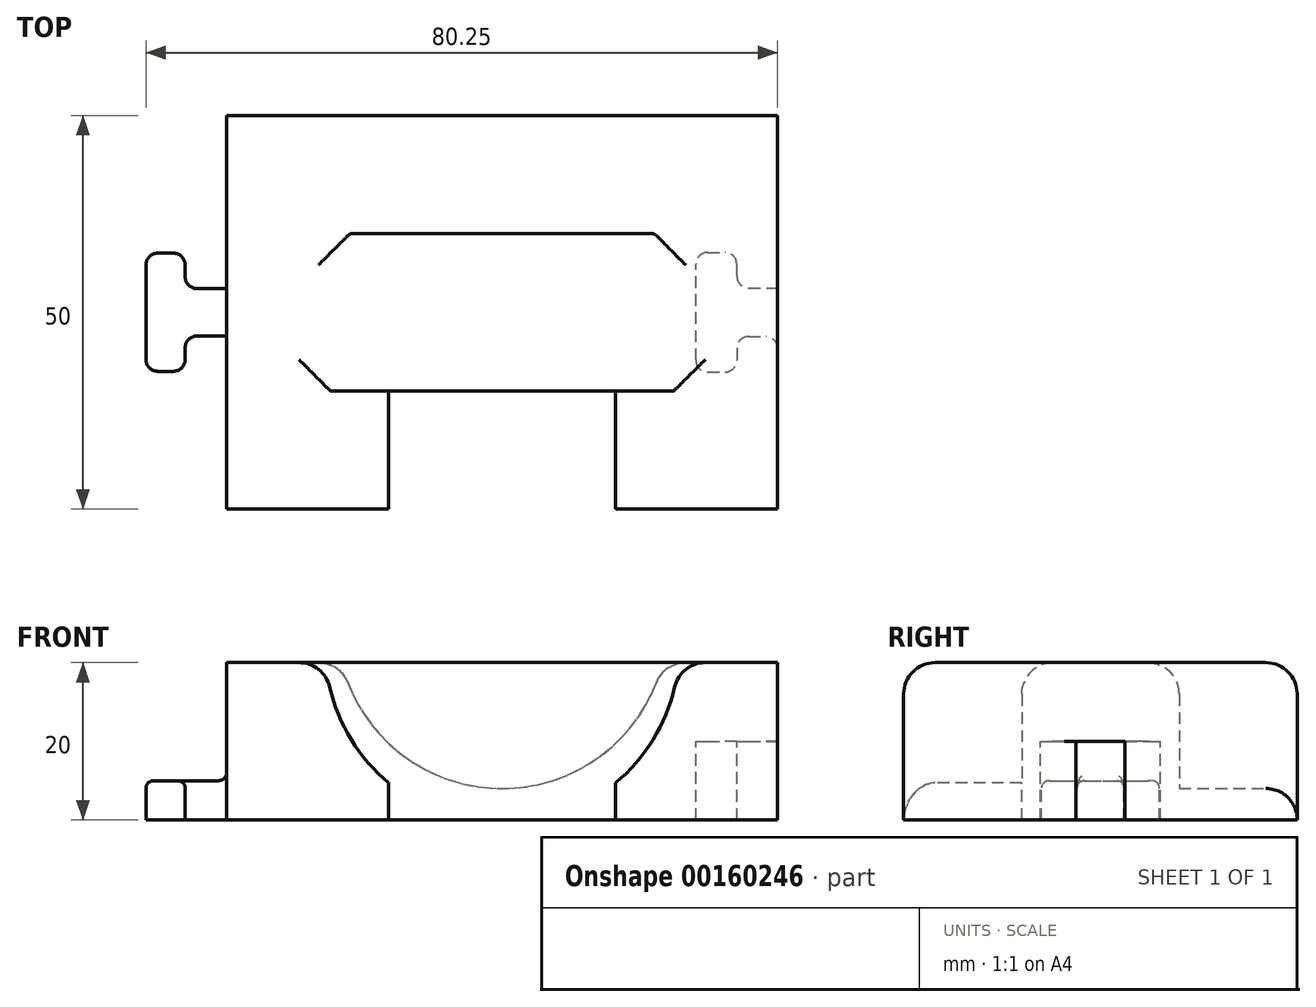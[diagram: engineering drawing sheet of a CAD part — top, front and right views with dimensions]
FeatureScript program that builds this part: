
annotation { "Feature Type Name" : "Feature", "Feature Type Description" : "" }
export const myFeature = defineFeature(function(context is Context, id is Id, definition is map)
    precondition{}
    {
        {
            var Q0;
            Q0=qCreatedBy(makeId("Top.planeOp"),FACE);
            var sketch = newSketch(context, id + "F0", { "sketchPlane" : qUnion([Q0])});
            skLineSegment(sketch, "E0.bottom", {"start": v(-30.59, 37.15) * mm, "end": v(39.41, 37.15) * mm});
            skLineSegment(sketch, "E0.top", {"start": v(-30.59, -12.85) * mm, "end": v(39.41, -12.85) * mm});
            skLineSegment(sketch, "E0.left", {"start": v(-30.59, 37.15) * mm, "end": v(-30.59, -12.85) * mm});
            skLineSegment(sketch, "E0.right", {"start": v(39.41, 37.15) * mm, "end": v(39.41, -12.85) * mm});
            skSolve(sketch);
        }
        {
            var Q0;
            Q0 = qSketchRegion(id + "F0", true);
            extrude(context, id + "F1", {"entities" : qUnion([Q0]), "depth" : 20 * mm});
        }
        {
            var Q0;
            Q0=makeQuery(id+"F1.opExtrude","SWEPT_FACE",FACE,{"disambiguationData":[OSD([sQuery(id+"F0.wireOp",EDGE,"E0.top")])]});
            var sketch = newSketch(context, id + "F2", { "sketchPlane" : qUnion([Q0])});
            skCircle(sketch, "E1", {"center": v(4.41, 22) * mm, "radius": 22.5 * mm});
            skPoint(sketch, "E1.centerSnap0", {"position": v(4.41, 20) * mm});
            skSolve(sketch);
        }
        {
            var Q0;
            Q0 = qSketchRegion(id + "F2", true);
            extrude(context, id + "F3", {"entities" : qUnion([Q0]), "operationType" : NewBodyOperationType.REMOVE, "oppositeDirection" : true, "depth" : 15 * mm});
        }
        {
            var Q0;
            Q0=makeQuery(id+"F1.opExtrude","SWEPT_FACE",FACE,{"disambiguationData":[OSD([sQuery(id+"F0.wireOp",EDGE,"E0.bottom")])]});
            var sketch = newSketch(context, id + "F4", { "sketchPlane" : qUnion([Q0])});
            skCircle(sketch, "E2", {"center": v(-4.41, 25) * mm, "radius": 21 * mm});
            skPoint(sketch, "E2.centerSnap0", {"position": v(-4.41, 25) * mm});
            skSolve(sketch);
        }
        {
            var Q0;
            Q0 = qSketchRegion(id + "F4", true);
            extrude(context, id + "F5", {"entities" : qUnion([Q0]), "operationType" : NewBodyOperationType.REMOVE, "oppositeDirection" : true, "depth" : 15 * mm});
        }
        {
            var Q0;
            Q0=makeQuery(id+"F1.opExtrude","CAP_FACE",FACE,{"disambiguationData":[OSD([sQuery(id+"F0.wireOp",EDGE,"E0.bottom"),sQuery(id+"F0.wireOp",EDGE,"E0.top"),sQuery(id+"F0.wireOp",EDGE,"E0.left"),sQuery(id+"F0.wireOp",EDGE,"E0.right")])],"isStart":false});
            var sketch = newSketch(context, id + "F6", { "sketchPlane" : qUnion([Q0])});
            skLineSegment(sketch, "E3.0", {"start": v(9.13, -12.85) * mm, "end": v(26.82, -12.85) * mm});
            skLineSegment(sketch, "E4.0", {"start": v(-18, -12.85) * mm, "end": v(-0.3, -12.85) * mm});
            skLineSegment(sketch, "E5.bottom", {"start": v(18.82, -12.85) * mm, "end": v(-10, -12.85) * mm});
            skLineSegment(sketch, "E5.top", {"start": v(18.82, 2.15) * mm, "end": v(-10, 2.15) * mm});
            skLineSegment(sketch, "E5.left", {"start": v(18.82, -12.85) * mm, "end": v(18.82, 2.15) * mm});
            skLineSegment(sketch, "E5.right", {"start": v(-10, -12.85) * mm, "end": v(-10, 2.15) * mm});
            skLineSegment(sketch, "E6", {"start": v(39.41, 12.15) * mm, "end": v(-30.59, 12.15) * mm, "construction": true});
            skLineSegment(sketch, "E7.bottom", {"start": v(39.41, 9.05) * mm, "end": v(29.01, 9.05) * mm});
            skLineSegment(sketch, "E7.top", {"start": v(39.41, 15.25) * mm, "end": v(29.01, 15.25) * mm});
            skLineSegment(sketch, "E7.left", {"start": v(39.41, 9.05) * mm, "end": v(39.41, 15.25) * mm});
            skLineSegment(sketch, "E7.right", {"start": v(29.01, 9.05) * mm, "end": v(29.01, 15.25) * mm});
            skPoint(sketch, "E8.oppositeSnap0", {"position": v(34.21, 15.25) * mm});
            skLineSegment(sketch, "E8.bottom", {"start": v(29.01, 4.55) * mm, "end": v(34.21, 4.55) * mm});
            skLineSegment(sketch, "E8.top", {"start": v(29.01, 19.75) * mm, "end": v(34.21, 19.75) * mm});
            skLineSegment(sketch, "E8.left", {"start": v(29.01, 4.55) * mm, "end": v(29.01, 19.75) * mm});
            skLineSegment(sketch, "E8.right", {"start": v(34.21, 4.55) * mm, "end": v(34.21, 19.75) * mm});
            skLineSegment(sketch, "E9.bottom", {"start": v(-30.59, 9.15) * mm, "end": v(-35.84, 9.15) * mm});
            skLineSegment(sketch, "E9.top", {"start": v(-30.59, 15.15) * mm, "end": v(-35.84, 15.15) * mm});
            skLineSegment(sketch, "E9.left", {"start": v(-30.59, 9.15) * mm, "end": v(-30.59, 15.15) * mm});
            skLineSegment(sketch, "E9.right", {"start": v(-35.84, 9.15) * mm, "end": v(-35.84, 15.15) * mm});
            skLineSegment(sketch, "E10.bottom", {"start": v(-35.84, 4.65) * mm, "end": v(-40.84, 4.65) * mm});
            skLineSegment(sketch, "E10.top", {"start": v(-35.84, 19.65) * mm, "end": v(-40.84, 19.65) * mm});
            skLineSegment(sketch, "E10.left", {"start": v(-35.84, 4.65) * mm, "end": v(-35.84, 19.65) * mm});
            skLineSegment(sketch, "E10.right", {"start": v(-40.84, 4.65) * mm, "end": v(-40.84, 19.65) * mm});
            skSolve(sketch);
        }
        {
            var Q0;
            {var subQ3=sQuery(id+"F6.wireOp",EDGE,"E10.bottom");Q0=makeQuery(id+"F6.imprint","IMPRINT",FACE,{"disambiguationData":[TD([[makeQuery(id+"F6.imprint","IMPRINT",EDGE,{"derivedFrom":subQ3}),-1.0]])]});}
            var Q1;
            {var subQ0=sQuery(id+"F6.wireOp",EDGE,"E9.bottom");Q1=makeQuery(id+"F6.imprint","IMPRINT",FACE,{"disambiguationData":[TD([[makeQuery(id+"F6.imprint","IMPRINT",EDGE,{"derivedFrom":subQ0}),-1.0]])]});}
            extrude(context, id + "F7", {"entities" : qUnion([Q0, Q1]), "operationType" : NewBodyOperationType.ADD, "oppositeDirection" : true, "depth" : 20 * mm});
        }
        {
            var Q0;
            Q0=makeQuery(id+"F6.imprint","IMPRINT",FACE,{"disambiguationData":[TD([[makeQuery(id+"F6.imprint","IMPRINT",EDGE,{"derivedFrom":sQuery(id+"F6.wireOp",EDGE,"E5.top")}),-1.0]])]});
            var Q1;
            {var subQ5=sQuery(id+"F6.wireOp",EDGE,"E8.bottom");Q1=makeQuery(id+"F6.imprint","IMPRINT",FACE,{"disambiguationData":[TD([[makeQuery(id+"F6.imprint","IMPRINT",EDGE,{"derivedFrom":subQ5}),1.0]])]});}
            var Q2;
            {var subQ0=sQuery(id+"F6.wireOp",EDGE,"E8.left");var subQ1=sQuery(id+"F6.wireOp",EDGE,"E7.bottom");var subQ2=makeQuery(id+"F6.imprint","INTERSECT",VERTEX,{"derivedFrom":[subQ1,subQ0]});Q2=makeQuery(id+"F6.imprint","IMPRINT",FACE,{"disambiguationData":[TD([[makeQuery(id+"F6.imprint","IMPRINT",EDGE,{"disambiguationData":[TD([[subQ2,1.0]])],"derivedFrom":subQ1}),-1.0]])]});}
            var Q3;
            {var subQ0=sQuery(id+"F6.wireOp",EDGE,"E7.left");Q3=makeQuery(id+"F6.imprint","IMPRINT",FACE,{"disambiguationData":[TD([[makeQuery(id+"F6.imprint","IMPRINT",EDGE,{"derivedFrom":subQ0}),-1.0]])]});}
            var Q4;
            {var subQ5=sQuery(id+"F6.wireOp",EDGE,"E8.top");Q4=makeQuery(id+"F6.imprint","IMPRINT",FACE,{"disambiguationData":[TD([[makeQuery(id+"F6.imprint","IMPRINT",EDGE,{"derivedFrom":subQ5}),-1.0]])]});}
            extrude(context, id + "F8", {"entities" : qUnion([Q0, Q1, Q2, Q3, Q4]), "operationType" : NewBodyOperationType.REMOVE, "oppositeDirection" : true, "depth" : 25 * mm});
        }
        {
            var Q0;
            Q0=makeQuery(id+"F15.opFillet","SPLIT",FACE,{"disambiguationData":[OD(0.0)],"derivedFrom":makeQuery(id+"F7.boolean.opBoolean","MERGE",FACE,{"derivedFrom":[makeQuery(id+"F1.opExtrude","CAP_FACE",FACE,{"disambiguationData":[OSD([sQuery(id+"F0.wireOp",EDGE,"E0.bottom"),sQuery(id+"F0.wireOp",EDGE,"E0.top"),sQuery(id+"F0.wireOp",EDGE,"E0.left"),sQuery(id+"F0.wireOp",EDGE,"E0.right")])],"isStart":false}),makeQuery(id+"F7.opExtrude","CAP_FACE",FACE,{"disambiguationData":[OSD([sQuery(id+"F6.wireOp",EDGE,"E9.bottom"),sQuery(id+"F6.wireOp",EDGE,"E9.top"),sQuery(id+"F6.wireOp",EDGE,"E9.left"),sQuery(id+"F6.wireOp",EDGE,"E10.bottom"),sQuery(id+"F6.wireOp",EDGE,"E10.top"),sQuery(id+"F6.wireOp",EDGE,"E10.left"),sQuery(id+"F6.wireOp",EDGE,"E10.right")])],"isStart":true})]})});
            var sketch = newSketch(context, id + "F9", { "sketchPlane" : qUnion([Q0])});
            skLineSegment(sketch, "E11.bottom", {"start": v(29.01, 4.55) * mm, "end": v(39.41, 4.55) * mm});
            skLineSegment(sketch, "E11.top", {"start": v(29.01, 19.75) * mm, "end": v(39.41, 19.75) * mm});
            skLineSegment(sketch, "E11.left", {"start": v(29.01, 4.55) * mm, "end": v(29.01, 19.75) * mm});
            skLineSegment(sketch, "E11.right", {"start": v(39.41, 4.55) * mm, "end": v(39.41, 19.75) * mm});
            skSolve(sketch);
        }
        {
            var Q0;
            Q0 = qSketchRegion(id + "F9", true);
            extrude(context, id + "F10", {"entities" : qUnion([Q0]), "operationType" : NewBodyOperationType.ADD, "oppositeDirection" : true, "depth" : 10 * mm});
        }
        {
            var Q0;
            Q0=makeQuery(id+"F8.boolean.opBoolean","COPY",EDGE,{"derivedFrom":makeQuery(id+"F8.opExtrude","SWEPT_EDGE",EDGE,{"disambiguationData":[OSD([sQuery(id+"F6.wireOp",EDGE,"E8.bottom"),sQuery(id+"F6.wireOp",EDGE,"E8.right")])]})});
            var Q1;
            Q1=makeQuery(id+"F8.boolean.opBoolean","COPY",EDGE,{"derivedFrom":makeQuery(id+"F8.opExtrude","SWEPT_EDGE",EDGE,{"disambiguationData":[OSD([sQuery(id+"F6.wireOp",EDGE,"E8.bottom"),sQuery(id+"F6.wireOp",EDGE,"E8.left")])]})});
            var Q2;
            Q2=makeQuery(id+"F8.boolean.opBoolean","COPY",EDGE,{"derivedFrom":makeQuery(id+"F8.opExtrude","SWEPT_EDGE",EDGE,{"disambiguationData":[OSD([sQuery(id+"F6.wireOp",EDGE,"E8.top"),sQuery(id+"F6.wireOp",EDGE,"E8.left")])]})});
            var Q3;
            Q3=makeQuery(id+"F8.boolean.opBoolean","COPY",EDGE,{"derivedFrom":makeQuery(id+"F8.opExtrude","SWEPT_EDGE",EDGE,{"disambiguationData":[OSD([sQuery(id+"F6.wireOp",EDGE,"E8.top"),sQuery(id+"F6.wireOp",EDGE,"E8.right")])]})});
            var Q4;
            Q4=makeQuery(id+"F8.boolean.opBoolean","COPY",EDGE,{"derivedFrom":makeQuery(id+"F8.opExtrude","SWEPT_EDGE",EDGE,{"disambiguationData":[OSD([sQuery(id+"F6.wireOp",EDGE,"E7.top"),sQuery(id+"F6.wireOp",EDGE,"E8.right")])]})});
            var Q5;
            Q5=makeQuery(id+"F8.boolean.opBoolean","COPY",EDGE,{"derivedFrom":makeQuery(id+"F8.opExtrude","SWEPT_EDGE",EDGE,{"disambiguationData":[OSD([sQuery(id+"F6.wireOp",EDGE,"E7.bottom"),sQuery(id+"F6.wireOp",EDGE,"E8.right")])]})});
            var Q6;
            Q6=makeQuery(id+"F7.opExtrude","SWEPT_EDGE",EDGE,{"disambiguationData":[OSD([sQuery(id+"F6.wireOp",EDGE,"E10.top"),sQuery(id+"F6.wireOp",EDGE,"E10.left")])]});
            var Q7;
            Q7=makeQuery(id+"F7.opExtrude","SWEPT_EDGE",EDGE,{"disambiguationData":[OSD([sQuery(id+"F6.wireOp",EDGE,"E10.top"),sQuery(id+"F6.wireOp",EDGE,"E10.right")])]});
            var Q8;
            Q8=makeQuery(id+"F7.opExtrude","SWEPT_EDGE",EDGE,{"disambiguationData":[OSD([sQuery(id+"F6.wireOp",EDGE,"E10.bottom"),sQuery(id+"F6.wireOp",EDGE,"E10.right")])]});
            var Q9;
            Q9=makeQuery(id+"F7.opExtrude","SWEPT_EDGE",EDGE,{"disambiguationData":[OSD([sQuery(id+"F6.wireOp",EDGE,"E10.bottom"),sQuery(id+"F6.wireOp",EDGE,"E10.left")])]});
            var Q10;
            Q10=makeQuery(id+"F7.opExtrude","SWEPT_EDGE",EDGE,{"disambiguationData":[OSD([sQuery(id+"F6.wireOp",EDGE,"E9.top"),sQuery(id+"F6.wireOp",EDGE,"E10.left")])]});
            var Q11;
            Q11=makeQuery(id+"F7.opExtrude","SWEPT_EDGE",EDGE,{"disambiguationData":[OSD([sQuery(id+"F6.wireOp",EDGE,"E9.bottom"),sQuery(id+"F6.wireOp",EDGE,"E10.left")])]});
            var Q12;
            Q12=makeQuery(id+"F8.boolean.opBoolean","COPY",EDGE,{"derivedFrom":makeQuery(id+"F8.opExtrude","SWEPT_EDGE",EDGE,{"disambiguationData":[OSD([sQuery(id+"F0.wireOp",EDGE,"E0.right"),sQuery(id+"F6.wireOp",EDGE,"E7.bottom"),sQuery(id+"F6.wireOp",EDGE,"E7.left")])]})});
            var Q13;
            Q13=makeQuery(id+"F8.boolean.opBoolean","COPY",EDGE,{"derivedFrom":makeQuery(id+"F8.opExtrude","SWEPT_EDGE",EDGE,{"disambiguationData":[OSD([sQuery(id+"F0.wireOp",EDGE,"E0.right"),sQuery(id+"F6.wireOp",EDGE,"E7.top"),sQuery(id+"F6.wireOp",EDGE,"E7.left")])]})});
            fillet(context, id + "F11", {"entities" : qUnion([Q0, Q1, Q2, Q3, Q4, Q5, Q6, Q7, Q8, Q9, Q10, Q11, Q12, Q13]), "radius" : 1.5 * mm, "tangentPropagation" : true, "allowEdgeOverflow" : false});
        }
        {
            var Q0;
            Q0=makeQuery(id+"F1.opExtrude","SWEPT_FACE",FACE,{"disambiguationData":[OSD([sQuery(id+"F0.wireOp",EDGE,"E0.bottom")])]});
            var sketch = newSketch(context, id + "F12", { "sketchPlane" : qUnion([Q0])});
            skLineSegment(sketch, "E12.bottom", {"start": v(30.59, 20) * mm, "end": v(41.94, 20) * mm});
            skLineSegment(sketch, "E12.top", {"start": v(30.59, 5) * mm, "end": v(41.94, 5) * mm});
            skLineSegment(sketch, "E12.left", {"start": v(30.59, 20) * mm, "end": v(30.59, 5) * mm});
            skLineSegment(sketch, "E12.right", {"start": v(41.94, 20) * mm, "end": v(41.94, 5) * mm});
            skSolve(sketch);
        }
        {
            var Q0;
            Q0=makeQuery(id+"F12.imprint","IMPRINT",FACE,{"disambiguationData":[TD([[makeQuery(id+"F12.imprint","IMPRINT",EDGE,{"derivedFrom":sQuery(id+"F12.wireOp",EDGE,"E12.bottom")}),-1.0]])]});
            extrude(context, id + "F13", {"entities" : qUnion([Q0]), "operationType" : NewBodyOperationType.REMOVE, "endBound" : BoundingType.THROUGH_ALL, "oppositeDirection" : true, "depth" : 25 * mm});
        }
        {
            var Q0;
            Q0=makeQuery(id+"F13.boolean.opBoolean","COPY",EDGE,{"derivedFrom":makeQuery(id+"F13.opExtrude","SWEPT_EDGE",EDGE,{"disambiguationData":[OSD([sQuery(id+"F0.wireOp",EDGE,"E0.bottom"),sQuery(id+"F0.wireOp",EDGE,"E0.left"),sQuery(id+"F12.wireOp",EDGE,"E12.top"),sQuery(id+"F12.wireOp",EDGE,"E12.left")])]})});
            fillet(context, id + "F14", {"entities" : qUnion([Q0]), "radius" : 1 * mm, "tangentPropagation" : true, "allowEdgeOverflow" : false});
        }
        {
            var Q0;
            Q0=makeQuery(id+"F5.boolean.opBoolean","INTERSECT",EDGE,{"disambiguationData":[OD(0.0)],"derivedFrom":[makeQuery(id+"F1.opExtrude","CAP_FACE",FACE,{"disambiguationData":[OSD([sQuery(id+"F0.wireOp",EDGE,"E0.bottom"),sQuery(id+"F0.wireOp",EDGE,"E0.top"),sQuery(id+"F0.wireOp",EDGE,"E0.left"),sQuery(id+"F0.wireOp",EDGE,"E0.right")])],"isStart":false}),makeQuery(id+"F5.opExtrude","SWEPT_FACE",FACE,{"disambiguationData":[OSD([sQuery(id+"F4.wireOp",EDGE,"E2")])]})]});
            var Q1;
            Q1=makeQuery(id+"F5.boolean.opBoolean","INTERSECT",EDGE,{"derivedFrom":[makeQuery(id+"F1.opExtrude","CAP_FACE",FACE,{"disambiguationData":[OSD([sQuery(id+"F0.wireOp",EDGE,"E0.bottom"),sQuery(id+"F0.wireOp",EDGE,"E0.top"),sQuery(id+"F0.wireOp",EDGE,"E0.left"),sQuery(id+"F0.wireOp",EDGE,"E0.right")])],"isStart":false}),makeQuery(id+"F5.opExtrude","CAP_FACE",FACE,{"disambiguationData":[OSD([sQuery(id+"F4.wireOp",EDGE,"E2")])],"isStart":false})]});
            var Q2;
            Q2=makeQuery(id+"F5.boolean.opBoolean","INTERSECT",EDGE,{"disambiguationData":[OD(1.0)],"derivedFrom":[makeQuery(id+"F1.opExtrude","CAP_FACE",FACE,{"disambiguationData":[OSD([sQuery(id+"F0.wireOp",EDGE,"E0.bottom"),sQuery(id+"F0.wireOp",EDGE,"E0.top"),sQuery(id+"F0.wireOp",EDGE,"E0.left"),sQuery(id+"F0.wireOp",EDGE,"E0.right")])],"isStart":false}),makeQuery(id+"F5.opExtrude","SWEPT_FACE",FACE,{"disambiguationData":[OSD([sQuery(id+"F4.wireOp",EDGE,"E2")])]})]});
            var Q3;
            Q3=makeQuery(id+"F3.boolean.opBoolean","INTERSECT",EDGE,{"disambiguationData":[OD(0.0)],"derivedFrom":[makeQuery(id+"F1.opExtrude","CAP_FACE",FACE,{"disambiguationData":[OSD([sQuery(id+"F0.wireOp",EDGE,"E0.bottom"),sQuery(id+"F0.wireOp",EDGE,"E0.top"),sQuery(id+"F0.wireOp",EDGE,"E0.left"),sQuery(id+"F0.wireOp",EDGE,"E0.right")])],"isStart":false}),makeQuery(id+"F3.opExtrude","SWEPT_FACE",FACE,{"disambiguationData":[OSD([sQuery(id+"F2.wireOp",EDGE,"E1")])]})]});
            var Q4;
            Q4=makeQuery(id+"F3.boolean.opBoolean","INTERSECT",EDGE,{"derivedFrom":[makeQuery(id+"F1.opExtrude","CAP_FACE",FACE,{"disambiguationData":[OSD([sQuery(id+"F0.wireOp",EDGE,"E0.bottom"),sQuery(id+"F0.wireOp",EDGE,"E0.top"),sQuery(id+"F0.wireOp",EDGE,"E0.left"),sQuery(id+"F0.wireOp",EDGE,"E0.right")])],"isStart":false}),makeQuery(id+"F3.opExtrude","CAP_FACE",FACE,{"disambiguationData":[OSD([sQuery(id+"F2.wireOp",EDGE,"E1")])],"isStart":false})]});
            var Q5;
            Q5=makeQuery(id+"F3.boolean.opBoolean","INTERSECT",EDGE,{"disambiguationData":[OD(1.0)],"derivedFrom":[makeQuery(id+"F1.opExtrude","CAP_FACE",FACE,{"disambiguationData":[OSD([sQuery(id+"F0.wireOp",EDGE,"E0.bottom"),sQuery(id+"F0.wireOp",EDGE,"E0.top"),sQuery(id+"F0.wireOp",EDGE,"E0.left"),sQuery(id+"F0.wireOp",EDGE,"E0.right")])],"isStart":false}),makeQuery(id+"F3.opExtrude","SWEPT_FACE",FACE,{"disambiguationData":[OSD([sQuery(id+"F2.wireOp",EDGE,"E1")])]})]});
            fillet(context, id + "F15", {"entities" : qUnion([Q0, Q1, Q2, Q3, Q4, Q5]), "radius" : 4 * mm, "tangentPropagation" : true, "allowEdgeOverflow" : false});
        }
        {
            var Q0;
            {var subQ0=sQuery(id+"F0.wireOp",EDGE,"E0.bottom");var subQ1=sQuery(id+"F0.wireOp",EDGE,"E0.right");Q0=makeQuery(id+"F5.boolean.opBoolean","SPLIT",EDGE,{"disambiguationData":[TD([makeQuery(id+"F1.opExtrude","SWEPT_FACE",FACE,{"disambiguationData":[OSD([subQ1])]})])],"derivedFrom":makeQuery(id+"F1.opExtrude","CAP_EDGE",EDGE,{"disambiguationData":[OSD([subQ0])],"isStart":false})});}
            var Q1;
            {var subQ0=sQuery(id+"F0.wireOp",EDGE,"E0.right");var subQ1=sQuery(id+"F0.wireOp",EDGE,"E0.top");Q1=makeQuery(id+"F3.boolean.opBoolean","SPLIT",EDGE,{"disambiguationData":[TD([makeQuery(id+"F1.opExtrude","SWEPT_FACE",FACE,{"disambiguationData":[OSD([subQ0])]})])],"derivedFrom":makeQuery(id+"F1.opExtrude","CAP_EDGE",EDGE,{"disambiguationData":[OSD([subQ1])],"isStart":false})});}
            var Q2;
            {var subQ0=sQuery(id+"F0.wireOp",EDGE,"E0.left");var subQ1=sQuery(id+"F0.wireOp",EDGE,"E0.top");Q2=makeQuery(id+"F3.boolean.opBoolean","SPLIT",EDGE,{"disambiguationData":[TD([makeQuery(id+"F1.opExtrude","SWEPT_FACE",FACE,{"disambiguationData":[OSD([subQ0])]})])],"derivedFrom":makeQuery(id+"F1.opExtrude","CAP_EDGE",EDGE,{"disambiguationData":[OSD([subQ1])],"isStart":false})});}
            fillet(context, id + "F16", {"entities" : qUnion([Q0, Q1, Q2]), "radius" : 4 * mm, "tangentPropagation" : true, "allowEdgeOverflow" : false});
        }
        {
            var Q0;
            Q0=makeQuery(id+"F13.boolean.opBoolean","INTERSECT",EDGE,{"derivedFrom":[makeQuery(id+"F11.opFillet","BLEND_FACE",FACE,{"disambiguationData":[OSD([sQuery(id+"F6.wireOp",EDGE,"E9.top"),sQuery(id+"F6.wireOp",EDGE,"E10.left")])]}),makeQuery(id+"F13.opExtrude","SWEPT_FACE",FACE,{"disambiguationData":[OSD([sQuery(id+"F12.wireOp",EDGE,"E12.top")])]})]});
            fillet(context, id + "F17", {"entities" : qUnion([Q0]), "radius" : 1 * mm, "tangentPropagation" : true, "allowEdgeOverflow" : false});
        }
    });
